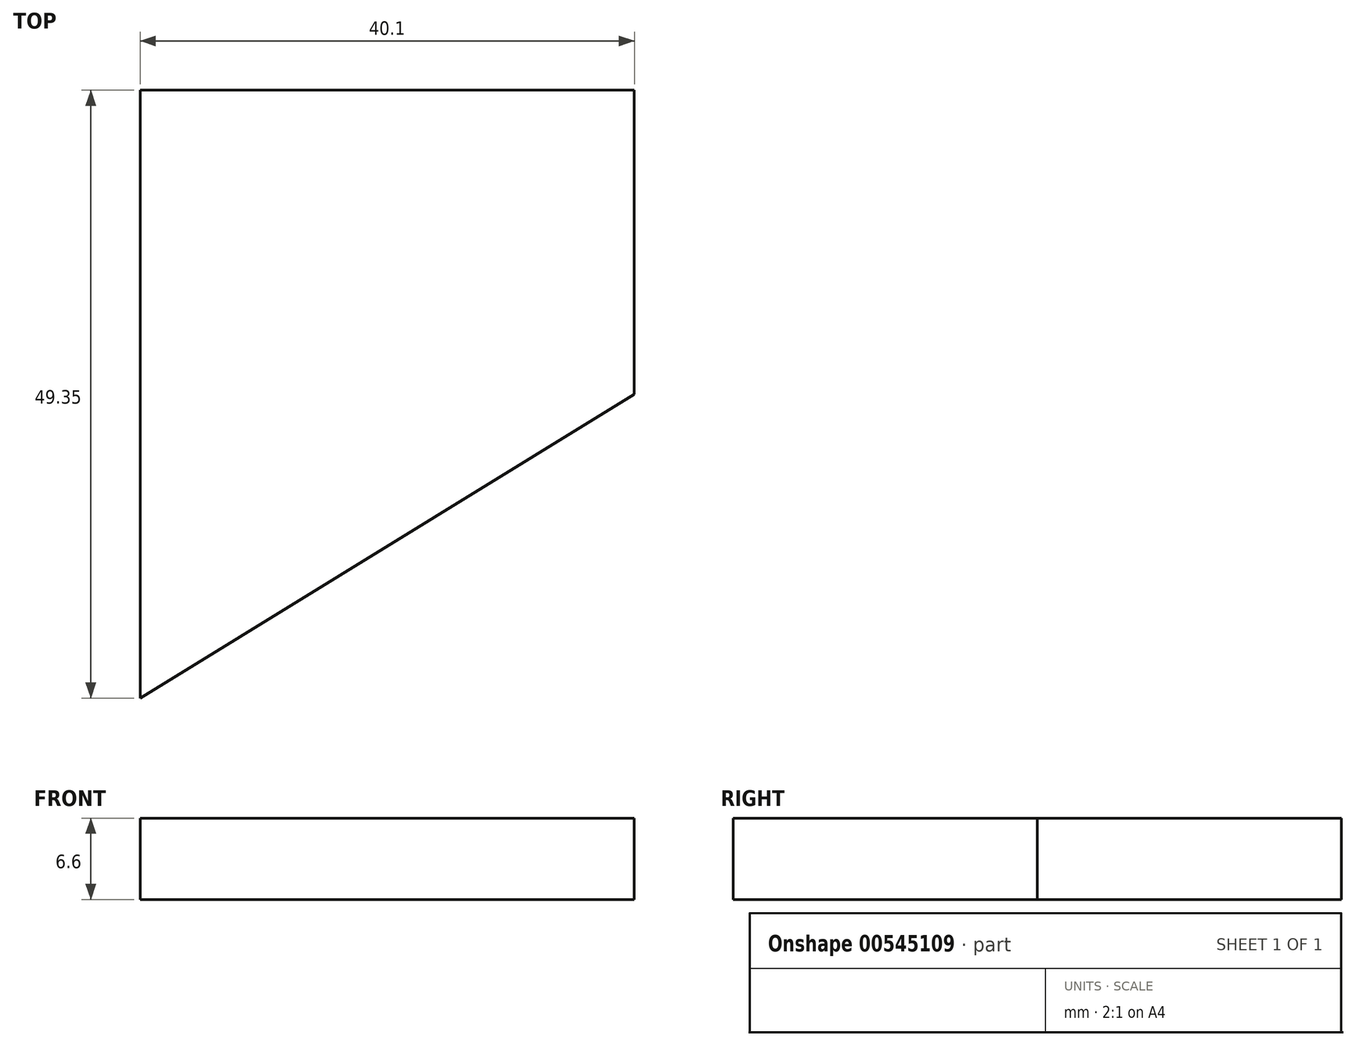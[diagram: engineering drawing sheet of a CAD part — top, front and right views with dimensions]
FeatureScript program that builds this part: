
annotation { "Feature Type Name" : "Feature", "Feature Type Description" : "" }
export const myFeature = defineFeature(function(context is Context, id is Id, definition is map)
    precondition{}
    {
        {
            var Q0;
            Q0=qCreatedBy(makeId("Top.planeOp"),FACE);
            var sketch = newSketch(context, id + "F0", { "sketchPlane" : qUnion([Q0])});
            skLineSegment(sketch, "E0", {"start": v(0, 0) * mm, "end": v(0, 49.35) * mm});
            skLineSegment(sketch, "E1", {"start": v(0, 49.35) * mm, "end": v(40.1, 49.35) * mm});
            skLineSegment(sketch, "E2", {"start": v(40.1, 49.35) * mm, "end": v(0, 24.67) * mm});
            skLineSegment(sketch, "E3", {"start": v(0, 24.67) * mm, "end": v(40.1, 24.67) * mm});
            skLineSegment(sketch, "E4", {"start": v(40.1, 24.67) * mm, "end": v(40.1, 49.35) * mm});
            skLineSegment(sketch, "E5", {"start": v(0, 0) * mm, "end": v(40.1, 24.67) * mm});
            skSolve(sketch);
        }
        {
            var Q0;
            Q0=makeQuery(id+"F0.imprint","IMPRINT",FACE,{"disambiguationData":[TD([[makeQuery(id+"F0.imprint","IMPRINT",EDGE,{"derivedFrom":sQuery(id+"F0.wireOp",EDGE,"E2")}),1.0]])]});
            var Q1;
            {var subQ2=sQuery(id+"F0.wireOp",EDGE,"E3");Q1=makeQuery(id+"F0.imprint","IMPRINT",FACE,{"disambiguationData":[TD([[makeQuery(id+"F0.imprint","IMPRINT",EDGE,{"derivedFrom":subQ2}),-1.0]])]});}
            var Q2;
            {var subQ0=sQuery(id+"F0.wireOp",EDGE,"E1");Q2=makeQuery(id+"F0.imprint","IMPRINT",FACE,{"disambiguationData":[TD([[makeQuery(id+"F0.imprint","IMPRINT",EDGE,{"derivedFrom":subQ0}),-1.0]])]});}
            extrude(context, id + "F1", {"entities" : qUnion([Q0, Q1, Q2]), "depth" : 6.6 * mm, "offsetDistance" : 25.4 * mm});
        }
    });
